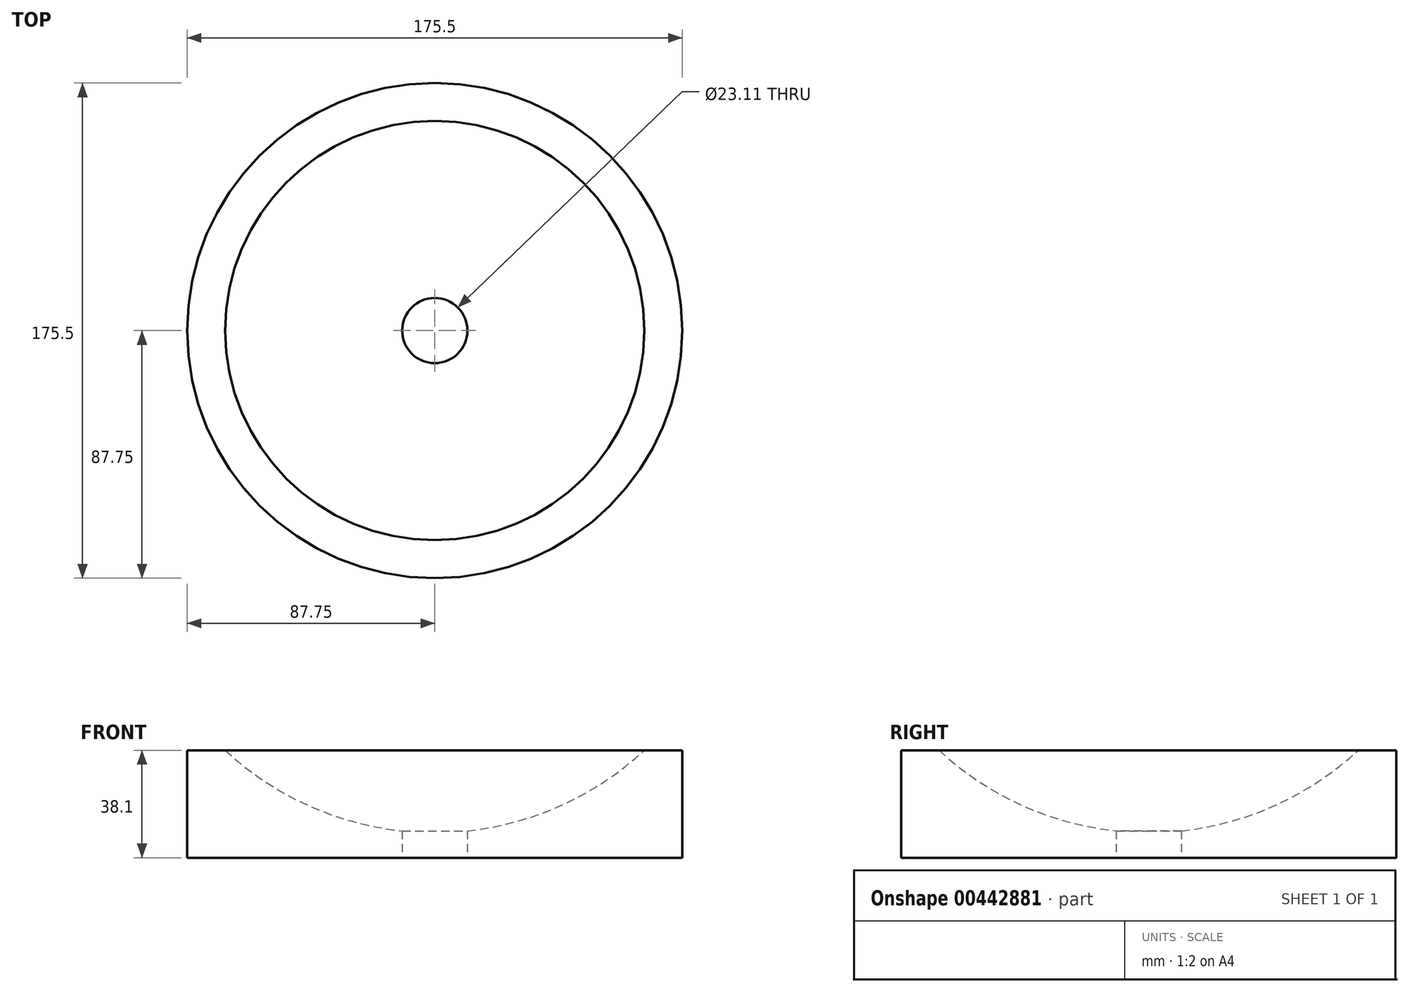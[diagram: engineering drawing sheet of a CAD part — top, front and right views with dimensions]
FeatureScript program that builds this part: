
annotation { "Feature Type Name" : "Feature", "Feature Type Description" : "" }
export const myFeature = defineFeature(function(context is Context, id is Id, definition is map)
    precondition{}
    {
        {
            var Q0;
            Q0=qCreatedBy(makeId("Front.planeOp"),FACE);
            var sketch = newSketch(context, id + "F0", { "sketchPlane" : qUnion([Q0])});
            skLineSegment(sketch, "E0", {"start": v(0, 0) * mm, "end": v(0, 108.73) * mm, "construction": true});
            skLineSegment(sketch, "E1", {"start": v(11.55, 0) * mm, "end": v(87.75, 0) * mm});
            skLineSegment(sketch, "E2", {"start": v(87.75, 0) * mm, "end": v(87.75, 38.1) * mm});
            skLineSegment(sketch, "E3", {"start": v(87.75, 38.1) * mm, "end": v(74.3, 38.1) * mm});
            skLineSegment(sketch, "E4", {"start": v(11.55, 0) * mm, "end": v(11.55, 9.53) * mm});
            skArc(sketch, "E5", {"start": v(11.55, 9.53) * mm, "mid": v(45.24, 18.73) * mm, "end": v(74.3, 38.1) * mm});
            skSolve(sketch);
        }
        {
            var Q0;
            Q0 = qSketchRegion(id + "F0", true);
            var Q1;
            Q1=sQuery(id+"F0.wireOp",EDGE,"E0");
            revolve(context, id + "F1", {"entities" : qUnion([Q0]), "axis" : qUnion([Q1]), "revolveType" : RevolveType.FULL});
        }
    });
